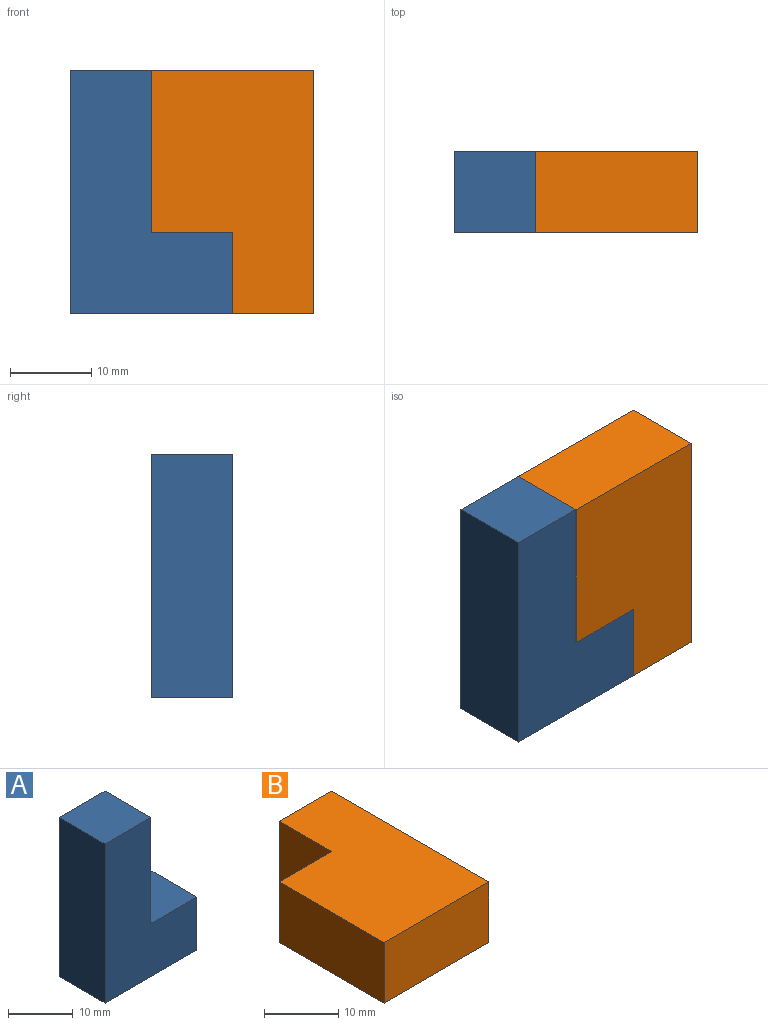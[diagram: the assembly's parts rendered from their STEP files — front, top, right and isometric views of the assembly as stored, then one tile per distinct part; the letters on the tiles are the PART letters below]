
ASSEMBLY  parts=2 mates=1
PART A: 8 faces, bbox 20x10x30 mm
  f0: plane 20x10mm, normal (1,0,0), area 200mm2, adj f1,f3,f4,f6
  f1: plane 30x20mm, normal (0,1,0), area 400mm2, adj f0,f2,f4,f5,f6,f7
  f2: plane 30x10mm, normal (-1,0,0), area 300mm2, adj f1,f3,f4,f5
  f3: plane 30x20mm, normal (0,-1,0), area 400mm2, adj f0,f2,f4,f5,f6,f7
  f4: plane 10x10mm, normal (0,0,1), area 100mm2, adj f0,f1,f2,f3
  f5: plane 20x10mm, normal (0,0,-1), area 200mm2, adj f1,f2,f3,f7
  f6: plane 10x10mm, normal (0,0,1), area 100mm2, adj f0,f1,f3,f7
  f7: plane 10x10mm, normal (1,0,0), area 100mm2, adj f1,f3,f5,f6
PART B: 8 faces, bbox 20x30x10 mm
  f0: plane 20x10mm, normal (-1,0,0), area 200mm2, adj f1,f5,f6,f7
  f1: plane 20x10mm, normal (0,-1,0), area 200mm2, adj f0,f2,f6,f7
  f2: plane 30x10mm, normal (1,0,0), area 300mm2, adj f1,f3,f6,f7
  f3: plane 10x10mm, normal (0,1,0), area 100mm2, adj f2,f4,f6,f7
  f4: plane 10x10mm, normal (-1,0,0), area 100mm2, adj f3,f5,f6,f7
  f5: plane 10x10mm, normal (0,1,0), area 100mm2, adj f0,f4,f6,f7
  f6: plane 30x20mm, normal (0,0,1), area 500mm2, adj f0,f1,f2,f3,f4,f5
  f7: plane 30x20mm, normal (0,0,-1), area 500mm2, adj f0,f1,f2,f3,f4,f5
PLACE A t=(-3.07,-5.72,-4.18)mm
PLACE B rot(axis=(-1,0,0),90deg) t=(16.36,-0.64,20.43)mm
MATE fastened B.f0 <-> A.f0  axis (-1,0,0) through (-4.93,4.36,15.82)mm
